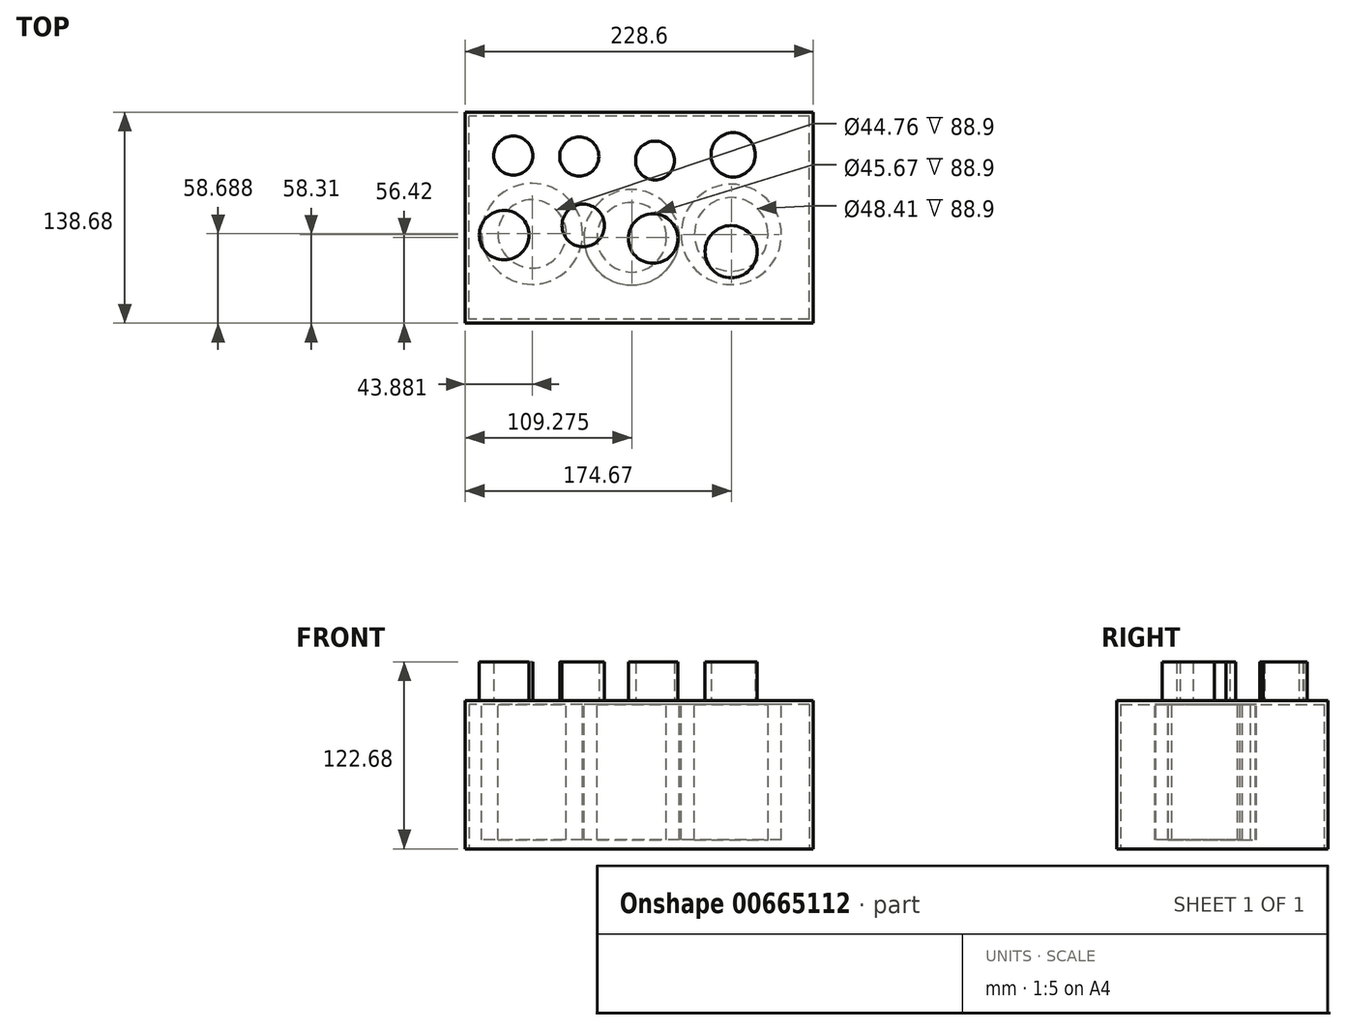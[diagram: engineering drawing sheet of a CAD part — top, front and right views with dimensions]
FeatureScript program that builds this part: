
annotation { "Feature Type Name" : "Feature", "Feature Type Description" : "" }
export const myFeature = defineFeature(function(context is Context, id is Id, definition is map)
    precondition{}
    {
        {
            var Q0;
            Q0=qCreatedBy(makeId("Right.planeOp"),FACE);
            var sketch = newSketch(context, id + "F0", { "sketchPlane" : qUnion([Q0])});
            skLineSegment(sketch, "E0.bottom", {"start": v(-123.96, 51.79) * mm, "end": v(14.72, 51.79) * mm});
            skLineSegment(sketch, "E0.top", {"start": v(-123.96, -45.5) * mm, "end": v(14.72, -45.5) * mm});
            skLineSegment(sketch, "E0.left", {"start": v(-123.96, 51.79) * mm, "end": v(-123.96, -45.5) * mm});
            skLineSegment(sketch, "E0.right", {"start": v(14.72, 51.79) * mm, "end": v(14.72, -45.5) * mm});
            skSolve(sketch);
        }
        {
            var Q0;
            Q0 = qSketchRegion(id + "F0", true);
            extrude(context, id + "F1", {"entities" : qUnion([Q0]), "depth" : 228.6 * mm, "offsetDistance" : 25.4 * mm});
        }
        {
            var Q0;
            Q0=makeQuery(id+"F1.opExtrude","SWEPT_FACE",FACE,{"disambiguationData":[OSD([sQuery(id+"F0.wireOp",EDGE,"E0.top")])]});
            shell(context, id + "F2", {"entities" : qUnion([Q0]), "thickness" : 2.54 * mm});
        }
        {
            var Q0;
            Q0=makeQuery(id+"F2.opShell","OFFSET_FACE",FACE,{"disambiguationData":[OSD([sQuery(id+"F0.wireOp",EDGE,"E0.bottom")])]});
            var sketch = newSketch(context, id + "F3", { "sketchPlane" : qUnion([Q0])});
            skCircle(sketch, "E1", {"center": v(43.88, 65.27) * mm, "radius": 33.14 * mm});
            skCircle(sketch, "E2", {"center": v(43.88, 65.27) * mm, "radius": 22.38 * mm});
            skSolve(sketch);
        }
        {
            var Q0;
            Q0 = qSketchRegion(id + "F3", true);
            extrude(context, id + "F4", {"entities" : qUnion([Q0]), "operationType" : NewBodyOperationType.ADD, "depth" : 88.9 * mm, "offsetDistance" : 25.4 * mm});
        }
        {
            var Q0;
            {var subQ1=sQuery(id+"F0.wireOp",EDGE,"E0.left");var subQ3=sQuery(id+"F0.wireOp",EDGE,"E0.bottom");Q0=makeQuery(id+"F4.boolean.opBoolean","SPLIT",FACE,{"disambiguationData":[TD([makeQuery(id+"F2.opShell","OFFSET_FACE",FACE,{"disambiguationData":[OSD([subQ1])]})])],"derivedFrom":makeQuery(id+"F2.opShell","OFFSET_FACE",FACE,{"disambiguationData":[OSD([subQ3])]})});}
            var sketch = newSketch(context, id + "F5", { "sketchPlane" : qUnion([Q0])});
            skCircle(sketch, "E3", {"center": v(109.28, 67.54) * mm, "radius": 31.37 * mm});
            skCircle(sketch, "E4", {"center": v(109.28, 67.54) * mm, "radius": 22.83 * mm});
            skSolve(sketch);
        }
        {
            var Q0;
            Q0 = qSketchRegion(id + "F5", true);
            extrude(context, id + "F6", {"entities" : qUnion([Q0]), "operationType" : NewBodyOperationType.ADD, "depth" : 88.9 * mm, "offsetDistance" : 25.4 * mm});
        }
        {
            var Q0;
            {var subQ2=sQuery(id+"F0.wireOp",EDGE,"E0.left");var subQ3=makeQuery(id+"F2.opShell","OFFSET_FACE",FACE,{"disambiguationData":[OSD([subQ2])]});var subQ5=sQuery(id+"F0.wireOp",EDGE,"E0.bottom");Q0=makeQuery(id+"F6.boolean.opBoolean","SPLIT",FACE,{"disambiguationData":[TD([subQ3])],"derivedFrom":makeQuery(id+"F4.boolean.opBoolean","SPLIT",FACE,{"disambiguationData":[TD([subQ3])],"derivedFrom":makeQuery(id+"F2.opShell","OFFSET_FACE",FACE,{"disambiguationData":[OSD([subQ5])]})})});}
            var sketch = newSketch(context, id + "F7", { "sketchPlane" : qUnion([Q0])});
            skCircle(sketch, "E5", {"center": v(174.67, 65.65) * mm, "radius": 32.92 * mm});
            skCircle(sketch, "E6", {"center": v(174.67, 65.65) * mm, "radius": 24.2 * mm});
            skSolve(sketch);
        }
        {
            var Q0;
            Q0 = qSketchRegion(id + "F7", true);
            extrude(context, id + "F8", {"entities" : qUnion([Q0]), "operationType" : NewBodyOperationType.ADD, "depth" : 88.9 * mm, "offsetDistance" : 25.4 * mm});
        }
        {
            var Q0;
            Q0=makeQuery(id+"F1.opExtrude","SWEPT_FACE",FACE,{"disambiguationData":[OSD([sQuery(id+"F0.wireOp",EDGE,"E0.bottom")])]});
            var sketch = newSketch(context, id + "F9", { "sketchPlane" : qUnion([Q0])});
            skCircle(sketch, "E7", {"center": v(31.56, -13.91) * mm, "radius": 12.84 * mm});
            skCircle(sketch, "E8", {"center": v(74.86, -14.45) * mm, "radius": 12.85 * mm});
            skCircle(sketch, "E9", {"center": v(124.58, -17.12) * mm, "radius": 12.75 * mm});
            skCircle(sketch, "E10", {"center": v(175.9, -13.38) * mm, "radius": 14.54 * mm});
            skCircle(sketch, "E11", {"center": v(174.58, -76.97) * mm, "radius": 17.13 * mm});
            skCircle(sketch, "E12", {"center": v(123.35, -68.34) * mm, "radius": 16.28 * mm});
            skCircle(sketch, "E13", {"center": v(77.46, -59.77) * mm, "radius": 13.96 * mm});
            skCircle(sketch, "E14", {"center": v(25.54, -66.11) * mm, "radius": 16.3 * mm});
            skSolve(sketch);
        }
        {
            var Q0;
            Q0 = qSketchRegion(id + "F9", true);
            extrude(context, id + "F10", {"entities" : qUnion([Q0]), "operationType" : NewBodyOperationType.ADD, "depth" : 25.4 * mm, "offsetDistance" : 25.4 * mm});
        }
    });
